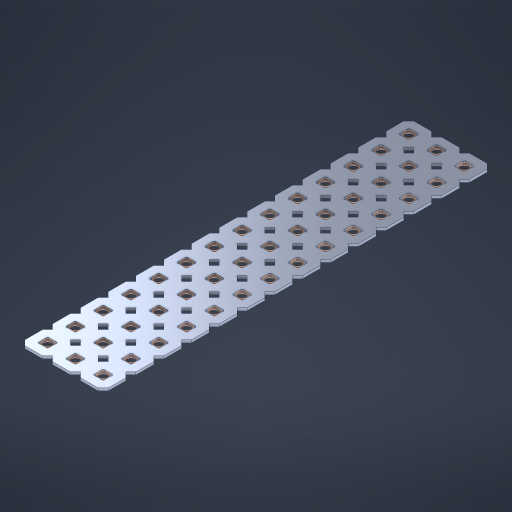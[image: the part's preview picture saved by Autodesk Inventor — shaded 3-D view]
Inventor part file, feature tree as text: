
AUTODESK INVENTOR PART (.ipt)
format: ipt  version: 2023 (Build 270158000, 158)  size: 741,376 bytes
history: native  units: in
note: dims shown in document units (in); Inventor stores cm internally (conversion verified against a paired STEP export)
features: other x43, extrude x41, sketch x2, pattern_linear x1
ambient origin geometry x8: Origin, YZ Plane, XZ Plane, XY Plane, X Axis, Y Axis, Z Axis, Center Point
bodies: Solid1 (feature_tree), Body (feature_tree)
feature tree (87):
  pattern_linear  "Rectangular Pattern1"  Spacing1=0.09in  [1 undecoded]
  sketch  "Sketch1"  dims[d1=0.5in]
  sketch  "Sketch2"  dims[d2=0.182in d3=0.09in d4=0.09in d5=0.09in d6=0.09in d7=0.09in d8=0.09in d9=0.09in d10=0.09in d11=0.02in d13=0.0in d14=0.172in d15=0.0625in d16=0.0in d19=0.5in d22=0.5in]
  other  "Srf1"
  other  "Srf126"
  other  "Srf127"
  other  "Srf128"
  other  "Srf129"
  other  "Srf130"
  other  "Srf131"
  other  "Srf250"
  other  "Srf251"
  other  "Srf252"
  other  "Srf253"
  other  "Srf254"
  other  "Srf255"
  other  "Srf256"
  other  "Srf268"
  other  "Srf269"
  other  "Srf270"
  other  "Srf271"
  other  "Srf272"
  other  "Srf273"
  other  "Srf274"
  other  "Srf275"
  other  "Srf276"
  other  "Srf277"
  other  "Srf278"
  other  "Srf279"
  other  "Srf280"
  other  "Srf281"
  other  "Srf293"
  other  "Srf294"
  other  "Srf295"
  other  "Srf296"
  other  "Srf297"
  other  "Srf298"
  other  "Srf299"
  other  "Srf300"
  other  "Srf301"
  other  "Srf302"
  other  "Srf303"
  other  "Srf304"
  other  "Srf305"
  other  "Srf306"
  other  "Circle"
  extrude  "ExtrusionSrf126"  Depth=0.09in
  extrude  "ExtrusionSrf127"  Depth=0.09in
  extrude  "ExtrusionSrf128"  Depth=0.09in
  extrude  "ExtrusionSrf129"  Depth=0.09in
  extrude  "ExtrusionSrf130"  Depth=0.09in
  extrude  "ExtrusionSrf131"  Depth=0.09in
  extrude  "ExtrusionSrf250"  Depth=0.09in
  extrude  "ExtrusionSrf251"  Depth=0.02in
  extrude  "ExtrusionSrf252"  TaperAngle=0.0deg  [1 undecoded]
  extrude  "ExtrusionSrf253"  Depth=0.5in
  extrude  "ExtrusionSrf254"  Depth=0.5in TaperAngle=0.0deg
  extrude  "ExtrusionSrf255"  Depth=0.5in
  extrude  "ExtrusionSrf256"  Depth=0.5in
  extrude  "ExtrusionSrf268"  [1 undecoded]
  extrude  "ExtrusionSrf269"  [1 undecoded]
  extrude  "ExtrusionSrf270"  [1 undecoded]
  extrude  "ExtrusionSrf271"  [1 undecoded]
  extrude  "ExtrusionSrf272"  [1 undecoded]
  extrude  "ExtrusionSrf273"  [1 undecoded]
  extrude  "ExtrusionSrf274"  [1 undecoded]
  extrude  "ExtrusionSrf275"  [1 undecoded]
  extrude  "ExtrusionSrf276"  [1 undecoded]
  extrude  "ExtrusionSrf277"  [1 undecoded]
  extrude  "ExtrusionSrf278"  [1 undecoded]
  extrude  "ExtrusionSrf279"  [1 undecoded]
  extrude  "ExtrusionSrf280"  [1 undecoded]
  extrude  "ExtrusionSrf281"  [1 undecoded]
  extrude  "ExtrusionSrf293"  [1 undecoded]
  extrude  "ExtrusionSrf294"  [1 undecoded]
  extrude  "ExtrusionSrf295"  [1 undecoded]
  extrude  "ExtrusionSrf296"  [1 undecoded]
  extrude  "ExtrusionSrf297"  [1 undecoded]
  extrude  "ExtrusionSrf298"  [1 undecoded]
  extrude  "ExtrusionSrf299"  [1 undecoded]
  extrude  "ExtrusionSrf300"  [1 undecoded]
  extrude  "ExtrusionSrf301"  [1 undecoded]
  extrude  "ExtrusionSrf302"  [1 undecoded]
  extrude  "ExtrusionSrf303"  [1 undecoded]
  extrude  "ExtrusionSrf304"  [1 undecoded]
  extrude  "ExtrusionSrf305"  [1 undecoded]
  extrude  "ExtrusionSrf306"  [1 undecoded]
note: 30 required parameter values undecoded (feature->parameter linkage not recoverable at this tier; creation-order binding heuristic only, values carry confidence <= 0.55)
